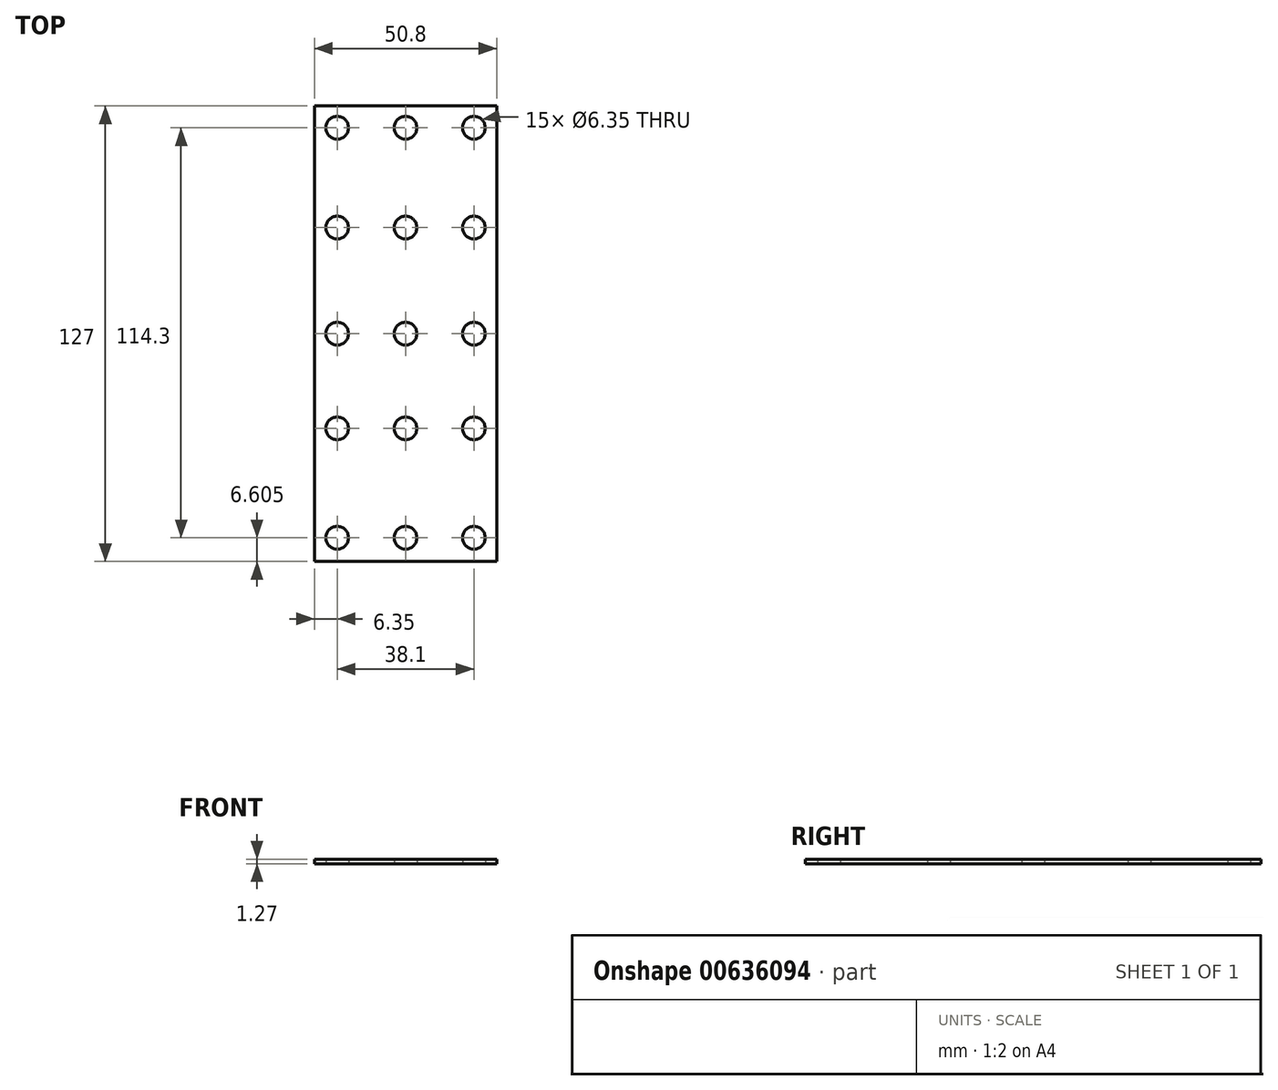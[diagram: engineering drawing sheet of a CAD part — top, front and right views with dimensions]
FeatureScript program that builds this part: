
annotation { "Feature Type Name" : "Feature", "Feature Type Description" : "" }
export const myFeature = defineFeature(function(context is Context, id is Id, definition is map)
    precondition{}
    {
        {
            var Q0;
            Q0=qCreatedBy(makeId("Top.planeOp"),FACE);
            var sketch = newSketch(context, id + "F0", { "sketchPlane" : qUnion([Q0])});
            skLineSegment(sketch, "E0.bottom", {"start": v(-25.4, 63.5) * mm, "end": v(25.4, 63.5) * mm});
            skLineSegment(sketch, "E0.top", {"start": v(-25.4, -63.5) * mm, "end": v(25.4, -63.5) * mm});
            skLineSegment(sketch, "E0.left", {"start": v(25.4, 63.5) * mm, "end": v(25.4, -63.5) * mm});
            skLineSegment(sketch, "E0.right", {"start": v(-25.4, 63.5) * mm, "end": v(-25.4, -63.5) * mm});
            skPoint(sketch, "E0.middle", {"position": v(0, 0) * mm});
            skSolve(sketch);
        }
        {
            var Q0;
            Q0=qSketchRegion(id+"F0",true);
            extrude(context, id + "F1", {"entities" : qUnion([Q0]), "depth" : 1.27 * mm});
        }
        {
            var Q0;
            Q0=qCreatedBy(makeId("Top.planeOp"),FACE);
            var sketch = newSketch(context, id + "F2", { "sketchPlane" : qUnion([Q0])});
            skPoint(sketch, "E1", {"position": v(0, 57.4) * mm});
            skPoint(sketch, "E2", {"position": v(19.05, 57.4) * mm});
            skPoint(sketch, "E3", {"position": v(-19.05, 57.4) * mm});
            skPoint(sketch, "E4", {"position": v(-19.05, 29.57) * mm});
            skPoint(sketch, "E5", {"position": v(0, 29.57) * mm});
            skPoint(sketch, "E6", {"position": v(19.05, 29.57) * mm});
            skPoint(sketch, "E7", {"position": v(19.05, 0) * mm});
            skPoint(sketch, "E8", {"position": v(-19.05, 0) * mm});
            skPoint(sketch, "E9", {"position": v(0, -26.4) * mm});
            skPoint(sketch, "E10", {"position": v(-19.05, -26.4) * mm});
            skPoint(sketch, "E11", {"position": v(-19.05, -56.9) * mm});
            skPoint(sketch, "E12", {"position": v(0, -56.9) * mm});
            skPoint(sketch, "E13", {"position": v(19.05, -56.9) * mm});
            skPoint(sketch, "E14", {"position": v(19.05, -26.4) * mm});
            skSolve(sketch);
        }
        {
            var Q0;
            Q0=sQuery(id+"F2.wireOp",VERTEX,"E3");
            var Q1;
            Q1=sQuery(id+"F2.wireOp",VERTEX,"E1");
            var Q2;
            Q2=sQuery(id+"F2.wireOp",VERTEX,"E2");
            var Q3;
            Q3=sQuery(id+"F2.wireOp",VERTEX,"E6");
            var Q4;
            Q4=sQuery(id+"F2.wireOp",VERTEX,"E5");
            var Q5;
            Q5=sQuery(id+"F2.wireOp",VERTEX,"E4");
            var Q6;
            Q6=sQuery(id+"F2.wireOp",VERTEX,"E8");
            var Q7;
            Q7=sQuery(id+"F0.wireOp",VERTEX,"E0.middle");
            var Q8;
            Q8=sQuery(id+"F2.wireOp",VERTEX,"E7");
            var Q9;
            Q9=sQuery(id+"F2.wireOp",VERTEX,"E14");
            var Q10;
            Q10=sQuery(id+"F2.wireOp",VERTEX,"E12");
            var Q11;
            Q11=sQuery(id+"F2.wireOp",VERTEX,"E9");
            var Q12;
            Q12=sQuery(id+"F2.wireOp",VERTEX,"E10");
            var Q13;
            Q13=sQuery(id+"F2.wireOp",VERTEX,"E11");
            var Q14;
            Q14=sQuery(id+"F2.wireOp",VERTEX,"E13");
            var Q15;
            Q15=makeQuery(id+"F1.opExtrude","SWEPT_BODY",BODY,{"disambiguationData":[OSD([sQuery(id+"F0.wireOp",EDGE,"E0.bottom"),sQuery(id+"F0.wireOp",EDGE,"E0.top"),sQuery(id+"F0.wireOp",EDGE,"E0.left"),sQuery(id+"F0.wireOp",EDGE,"E0.right")])]});
            hole(context, id + "F3", {"style" : HoleStyle.SIMPLE, "endStyle" : HoleEndStyle.THROUGH, "oppositeDirection" : true, "holeDiameter" : 6.35 * mm, "majorDiameter" : 6.35 * mm, "isTappedThrough" : true, "tappedDepth" : 12.7 * mm, "tapClearance" : 3, "locations" : qUnion([Q0, Q1, Q2, Q3, Q4, Q5, Q6, Q7, Q8, Q9, Q10, Q11, Q12, Q13, Q14]), "scope" : qUnion([Q15])});
        }
    });
